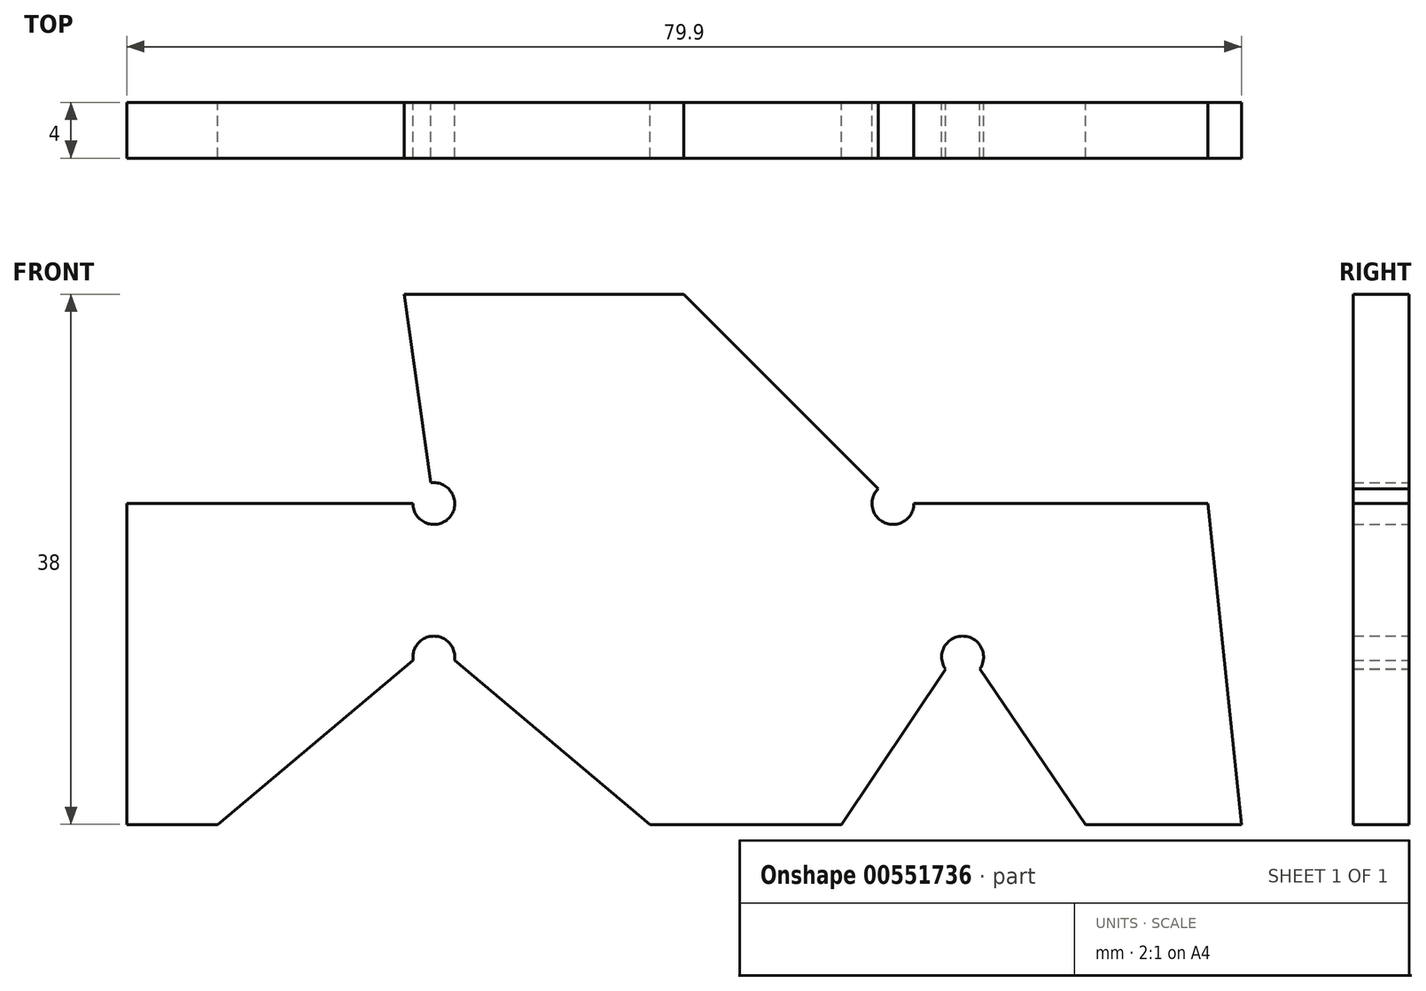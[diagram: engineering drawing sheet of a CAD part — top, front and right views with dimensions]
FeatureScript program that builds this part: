
annotation { "Feature Type Name" : "Feature", "Feature Type Description" : "" }
export const myFeature = defineFeature(function(context is Context, id is Id, definition is map)
    precondition{}
    {
        {
            var Q0;
            Q0=qCreatedBy(makeId("Front.planeOp"),FACE);
            var sketch = newSketch(context, id + "F0", { "sketchPlane" : qUnion([Q0])});
            skLineSegment(sketch, "E0.bottom", {"start": v(-39.62, 12.05) * mm, "end": v(-19.6, 12.05) * mm});
            skLineSegment(sketch, "E0.top", {"start": v(-59.5, -25.95) * mm, "end": v(-53, -25.95) * mm});
            skLineSegment(sketch, "E0.left", {"start": v(-59.5, -2.95) * mm, "end": v(-59.5, -25.95) * mm});
            skLineSegment(sketch, "E1", {"start": v(-22, -25.95) * mm, "end": v(-8.3, -25.95) * mm});
            skLineSegment(sketch, "E2", {"start": v(9.2, -25.95) * mm, "end": v(20.4, -25.95) * mm});
            skLineSegment(sketch, "E3", {"start": v(-59.5, -25.95) * mm, "end": v(-59.5, -2.95) * mm});
            skLineSegment(sketch, "E4", {"start": v(-59.5, -2.95) * mm, "end": v(-39, -2.95) * mm});
            skLineSegment(sketch, "E5", {"start": v(17.97, -2.95) * mm, "end": v(-3.1, -2.95) * mm});
            skLineSegment(sketch, "E6", {"start": v(-5.67, -1.9) * mm, "end": v(-19.6, 12.05) * mm});
            skLineSegment(sketch, "E7", {"start": v(20.4, -25.95) * mm, "end": v(17.97, -2.95) * mm});
            skLineSegment(sketch, "E8", {"start": v(-37.72, -1.47) * mm, "end": v(-39.62, 12.05) * mm});
            skLineSegment(sketch, "E9", {"start": v(-53, -25.95) * mm, "end": v(-38.99, -14.2) * mm});
            skLineSegment(sketch, "E10", {"start": v(-36.03, -14.2) * mm, "end": v(-22, -25.95) * mm});
            skPoint(sketch, "E11.endSnap0", {"position": v(0.44, -25.95) * mm});
            skLineSegment(sketch, "E12", {"start": v(-0.84, -14.81) * mm, "end": v(-8.3, -25.95) * mm});
            skLineSegment(sketch, "E13", {"start": v(1.62, -14.8) * mm, "end": v(9.2, -25.95) * mm});
            skArc(sketch, "E14", {"start": v(-36.03, -14.2) * mm, "mid": v(-37.5, -12.45) * mm, "end": v(-38.99, -14.2) * mm});
            skArc(sketch, "E15", {"start": v(1.62, -14.8) * mm, "mid": v(0.38, -12.45) * mm, "end": v(-0.84, -14.81) * mm});
            skPoint(sketch, "E16.orphan", {"position": v(0.39, -12.98) * mm});
            skPoint(sketch, "E17.orphan", {"position": v(-37.5, -25.95) * mm});
            skArc(sketch, "E18", {"start": v(-39, -2.95) * mm, "mid": v(-36.38, -3.94) * mm, "end": v(-37.72, -1.47) * mm});
            skArc(sketch, "E19", {"start": v(-5.67, -1.9) * mm, "mid": v(-5.18, -4.34) * mm, "end": v(-3.1, -2.95) * mm});
            skSolve(sketch);
        }
        {
            var Q0;
            Q0 = qSketchRegion(id + "F0", true);
            extrude(context, id + "F1", {"entities" : qUnion([Q0]), "depth" : 4 * mm, "offsetDistance" : 25 * mm});
        }
    });
